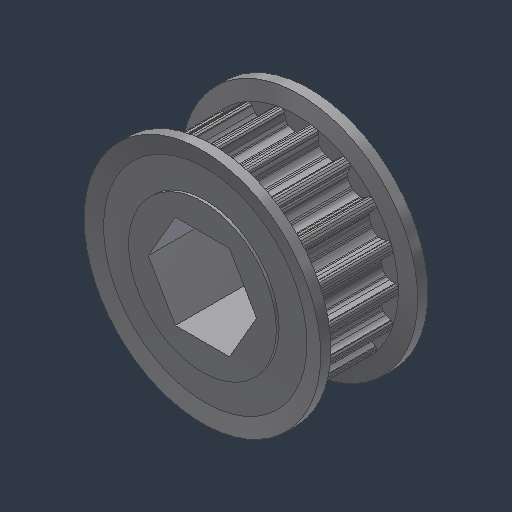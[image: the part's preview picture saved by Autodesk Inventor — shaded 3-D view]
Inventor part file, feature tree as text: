
AUTODESK INVENTOR PART (.ipt)
format: ipt  version: 2024.3 (Build 283343000, 343)  size: 467,456 bytes
history: native  units: mm (DEFAULTED — no unit token found)
features: mirror x1
ambient origin geometry x8: Origin, YZ Plane, XZ Plane, XY Plane, X Axis, Y Axis, Z Axis, Center Point
bodies: Solid1 (feature_tree)
feature tree (1):
  mirror  "Mirror1"
